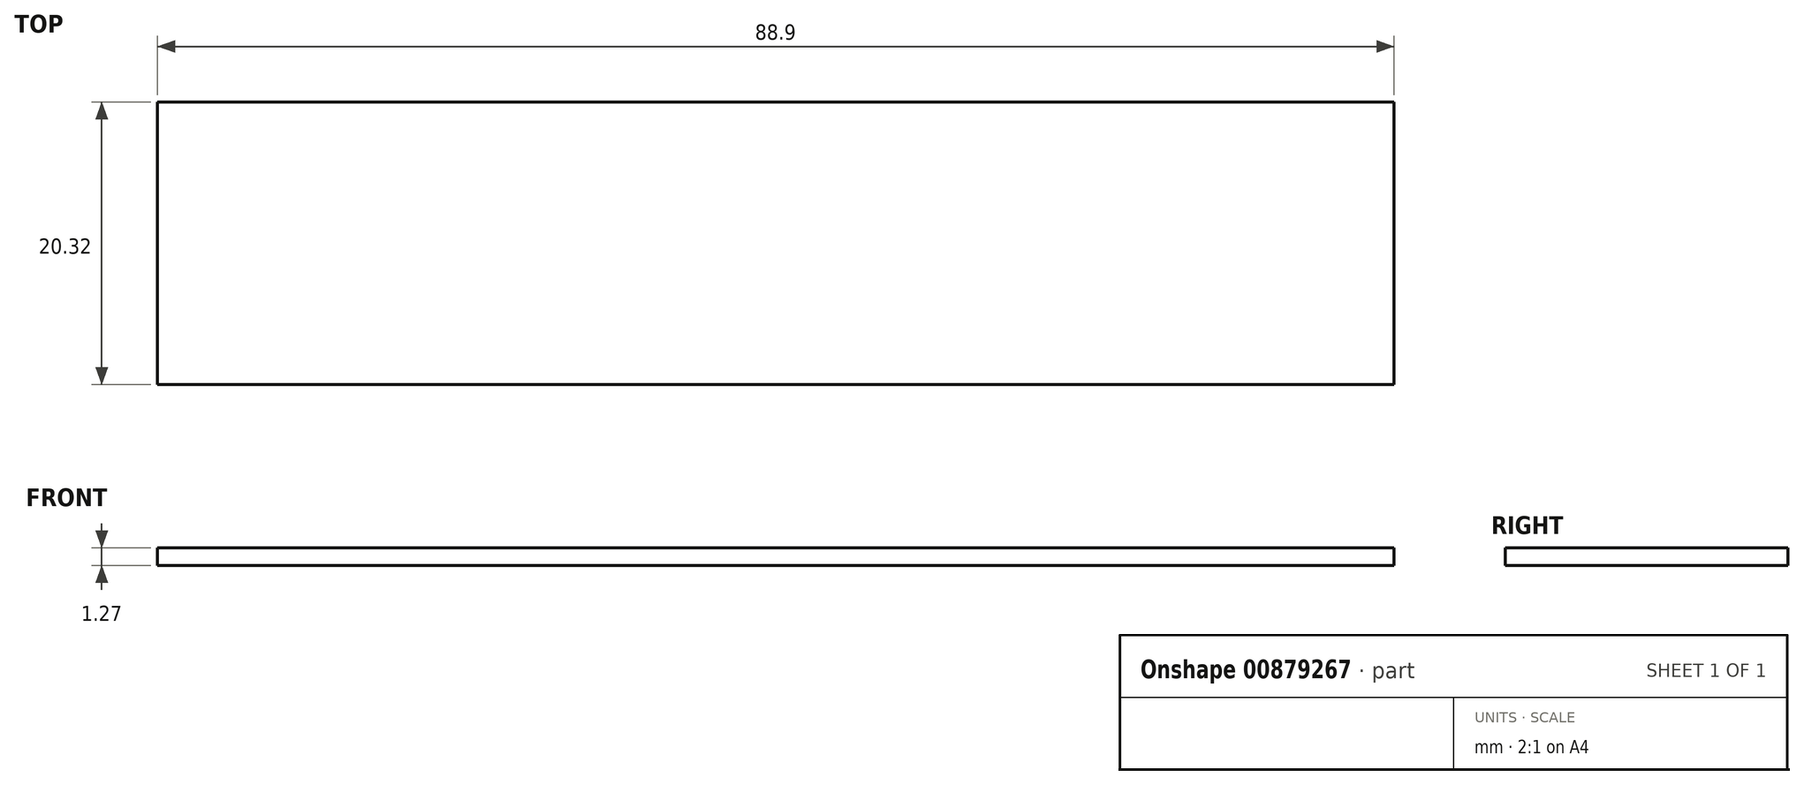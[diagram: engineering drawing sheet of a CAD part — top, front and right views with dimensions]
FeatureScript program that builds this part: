
annotation { "Feature Type Name" : "Feature", "Feature Type Description" : "" }
export const myFeature = defineFeature(function(context is Context, id is Id, definition is map)
    precondition{}
    {
        {
            var Q0;
            Q0=qCreatedBy(makeId("Top.planeOp"),FACE);
            var sketch = newSketch(context, id + "F0", { "sketchPlane" : qUnion([Q0])});
            skLineSegment(sketch, "E0.bottom", {"start": v(-53.63, -20.32) * mm, "end": v(35.27, -20.32) * mm});
            skLineSegment(sketch, "E0.top", {"start": v(-53.63, 0) * mm, "end": v(35.27, 0) * mm});
            skLineSegment(sketch, "E0.left", {"start": v(-53.63, -20.32) * mm, "end": v(-53.63, 0) * mm});
            skLineSegment(sketch, "E0.right", {"start": v(35.27, -20.32) * mm, "end": v(35.27, 0) * mm});
            skSolve(sketch);
        }
        {
            var Q0;
            Q0=makeQuery(id+"F0.imprint","IMPRINT",FACE,{"disambiguationData":[TD([[makeQuery(id+"F0.imprint","IMPRINT",EDGE,{"derivedFrom":sQuery(id+"F0.wireOp",EDGE,"E0.bottom")}),1.0]])]});
            extrude(context, id + "F1", {"entities" : qUnion([Q0]), "depth" : 1.27 * mm, "offsetDistance" : 25.4 * mm});
        }
    });
